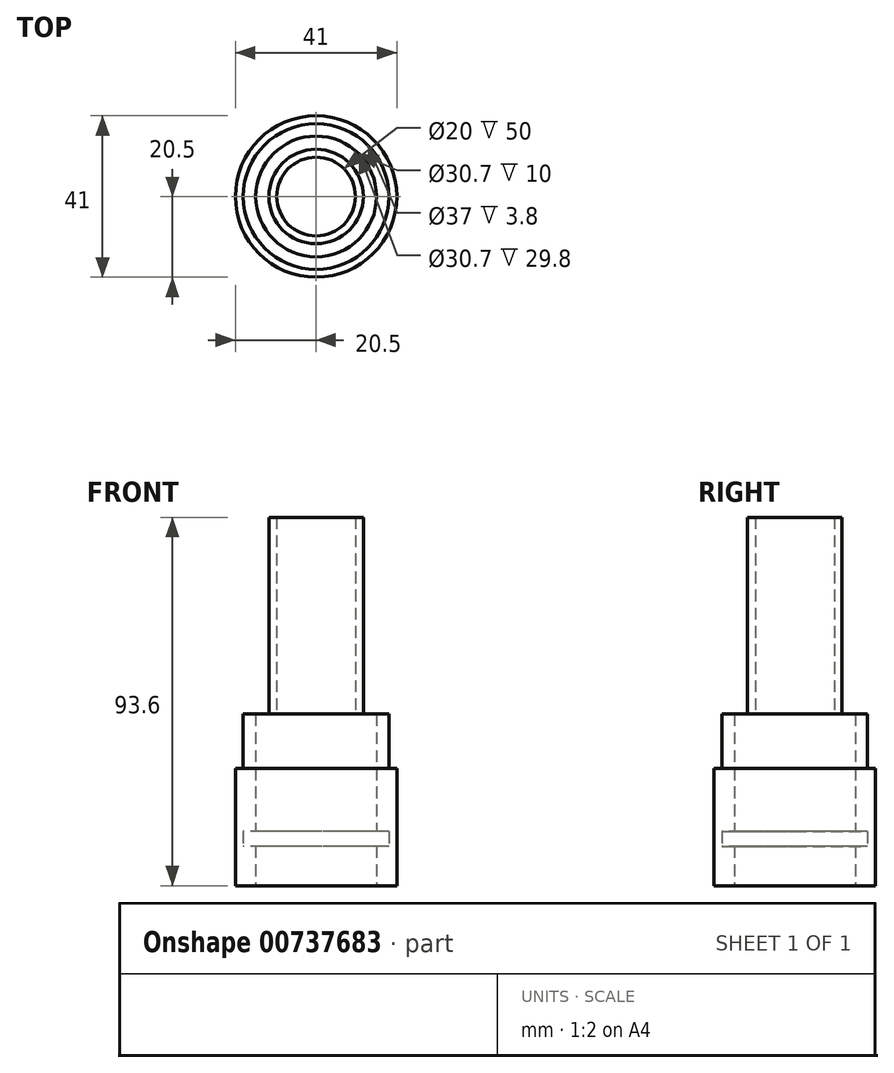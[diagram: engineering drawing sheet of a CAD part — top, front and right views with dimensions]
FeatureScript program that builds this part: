
annotation { "Feature Type Name" : "Feature", "Feature Type Description" : "" }
export const myFeature = defineFeature(function(context is Context, id is Id, definition is map)
    precondition{}
    {
        {
            var Q0;
            Q0=qCreatedBy(makeId("Top.planeOp"),FACE);
            var sketch = newSketch(context, id + "F0", { "sketchPlane" : qUnion([Q0])});
            skCircle(sketch, "E0", {"center": v(0, 0) * mm, "radius": 20.5 * mm});
            skCircle(sketch, "E1", {"center": v(0, 0) * mm, "radius": 15.35 * mm});
            skSolve(sketch);
        }
        {
            var Q0;
            Q0=makeQuery(id+"F0.imprint","IMPRINT",FACE,{"disambiguationData":[TD([[makeQuery(id+"F0.imprint","IMPRINT",EDGE,{"derivedFrom":sQuery(id+"F0.wireOp",EDGE,"E0")}),1.0]])]});
            extrude(context, id + "F1", {"entities" : qUnion([Q0]), "depth" : 10 * mm, "offsetDistance" : 25 * mm});
        }
        {
            var Q0;
            Q0=makeQuery(id+"F1.opExtrude","CAP_FACE",FACE,{"disambiguationData":[OSD([sQuery(id+"F0.wireOp",EDGE,"E0"),sQuery(id+"F0.wireOp",EDGE,"E1")])],"isStart":false});
            var sketch = newSketch(context, id + "F2", { "sketchPlane" : qUnion([Q0])});
            skCircle(sketch, "E2", {"center": v(0, 0) * mm, "radius": 18.5 * mm});
            skSolve(sketch);
        }
        {
            var Q0;
            Q0=makeQuery(id+"F2.imprint","IMPRINT",FACE,{"disambiguationData":[TD([[makeQuery(id+"F2.imprint","IMPRINT",EDGE,{"derivedFrom":sQuery(id+"F2.wireOp",EDGE,"E2")}),-1.0]])]});
            extrude(context, id + "F3", {"entities" : qUnion([Q0]), "operationType" : NewBodyOperationType.ADD, "depth" : 3.8 * mm, "offsetDistance" : 25 * mm});
        }
        {
            var Q0;
            Q0=makeQuery(id+"F3.opExtrude","CAP_FACE",FACE,{"disambiguationData":[OSD([sQuery(id+"F0.wireOp",EDGE,"E0"),sQuery(id+"F2.wireOp",EDGE,"E2")])],"isStart":false});
            var sketch = newSketch(context, id + "F4", { "sketchPlane" : qUnion([Q0])});
            skCircle(sketch, "E3", {"center": v(0, 0) * mm, "radius": 15.35 * mm});
            skSolve(sketch);
        }
        {
            var Q0;
            Q0=makeQuery(id+"F4.imprint","IMPRINT",FACE,{"disambiguationData":[TD([[makeQuery(id+"F4.imprint","IMPRINT",EDGE,{"derivedFrom":sQuery(id+"F4.wireOp",EDGE,"E3")}),-1.0]])]});
            var Q1;
            Q1=makeQuery(id+"F4.imprint","IMPRINT",FACE,{"disambiguationData":[TD([[makeQuery(id+"F4.imprint","IMPRINT",EDGE,{"derivedFrom":makeQuery(id+"F3.opExtrude","CAP_EDGE",EDGE,{"disambiguationData":[OSD([sQuery(id+"F2.wireOp",EDGE,"E2")])],"isStart":false})}),-1.0]])]});
            extrude(context, id + "F5", {"entities" : qUnion([Q0, Q1]), "operationType" : NewBodyOperationType.ADD, "depth" : 16 * mm, "offsetDistance" : 25 * mm});
        }
        {
            var Q0;
            Q0=makeQuery(id+"F5.opExtrude","CAP_FACE",FACE,{"disambiguationData":[OSD([sQuery(id+"F0.wireOp",EDGE,"E0"),sQuery(id+"F4.wireOp",EDGE,"E3")])],"isStart":false});
            var sketch = newSketch(context, id + "F6", { "sketchPlane" : qUnion([Q0])});
            skCircle(sketch, "E4", {"center": v(0, 0) * mm, "radius": 18.5 * mm});
            skSolve(sketch);
        }
        {
            var Q0;
            Q0=makeQuery(id+"F6.imprint","IMPRINT",FACE,{"disambiguationData":[TD([[makeQuery(id+"F6.imprint","IMPRINT",EDGE,{"derivedFrom":sQuery(id+"F6.wireOp",EDGE,"E4")}),1.0]])]});
            extrude(context, id + "F7", {"entities" : qUnion([Q0]), "operationType" : NewBodyOperationType.ADD, "depth" : 3.8 * mm, "offsetDistance" : 25 * mm});
        }
        {
            var Q0;
            Q0=makeQuery(id+"F7.opExtrude","CAP_FACE",FACE,{"disambiguationData":[OSD([sQuery(id+"F0.wireOp",EDGE,"E0"),sQuery(id+"F6.wireOp",EDGE,"E4")])],"isStart":false});
            var sketch = newSketch(context, id + "F8", { "sketchPlane" : qUnion([Q0])});
            skCircle(sketch, "E5", {"center": v(0, 0) * mm, "radius": 15.35 * mm});
            skSolve(sketch);
        }
        {
            var Q0;
            Q0=makeQuery(id+"F8.imprint","IMPRINT",FACE,{"disambiguationData":[TD([[makeQuery(id+"F8.imprint","IMPRINT",EDGE,{"derivedFrom":makeQuery(id+"F7.opExtrude","CAP_EDGE",EDGE,{"disambiguationData":[OSD([sQuery(id+"F6.wireOp",EDGE,"E4")])],"isStart":false})}),1.0]])]});
            var Q1;
            Q1=makeQuery(id+"F8.imprint","IMPRINT",FACE,{"disambiguationData":[TD([[makeQuery(id+"F8.imprint","IMPRINT",EDGE,{"derivedFrom":sQuery(id+"F8.wireOp",EDGE,"E5")}),-1.0]])]});
            extrude(context, id + "F9", {"entities" : qUnion([Q0, Q1]), "operationType" : NewBodyOperationType.ADD, "depth" : 10 * mm, "offsetDistance" : 25 * mm});
        }
        {
            var Q0;
            Q0=makeQuery(id+"F9.opExtrude","CAP_FACE",FACE,{"disambiguationData":[OSD([sQuery(id+"F0.wireOp",EDGE,"E0"),sQuery(id+"F8.wireOp",EDGE,"E5")])],"isStart":false});
            var sketch = newSketch(context, id + "F10", { "sketchPlane" : qUnion([Q0])});
            skCircle(sketch, "E6", {"center": v(0, 0) * mm, "radius": 12 * mm});
            skCircle(sketch, "E7", {"center": v(0, 0) * mm, "radius": 10 * mm});
            skSolve(sketch);
        }
        {
            var Q0;
            Q0=makeQuery(id+"F10.imprint","IMPRINT",FACE,{"disambiguationData":[TD([[makeQuery(id+"F10.imprint","IMPRINT",EDGE,{"derivedFrom":sQuery(id+"F10.wireOp",EDGE,"E6")}),1.0]])]});
            extrude(context, id + "F11", {"entities" : qUnion([Q0]), "depth" : 50 * mm, "offsetDistance" : 25 * mm});
        }
    });
